# Revit family: NLRS_63_LF_UN_noodverlichting Hillux_htk
name_source: partatom
category: Lighting Fixtures
units: mm (PartAtom-declared; Revit-internal decimal feet)

## family parameters
Always vertical = No
Cut with Voids When Loaded = No
Light Source = Yes
OmniClass Number = 23.80.70.11.21
OmniClass Title = Emergency Lighting
Part Type = Normal
Room Calculation Point = No
Round Connector Dimension = Use Diameter
Shared = Yes
Work Plane-Based = No

## types (1)
- Hillux LED Series 3 dec AT opbouw_NMD720-3
    Color Filter = 16777215
    Default Elevation = 0 mm  [stored 0 ft]
    Dimming Lamp Color Temperature Shift = <None>
    Emit Shape Visible in Rendering = Yes
    Emit from Circle Diameter = 610 mm
    Lamp = LED
    Manufacturer = Hertek
    Model = Hillux LED
    NLRS_C_breedte = 118 mm
    NLRS_C_breedte1 = 111 mm
    NLRS_C_code_artikel = NMB720-3
    NLRS_C_code_fabrikant_gln = 8714253082646
    NLRS_C_content_datum_uitgifte = 01-08-2022
    NLRS_C_content_versie = 1.0
    NLRS_C_diameter = 0 mm  [stored 0 ft]
    NLRS_C_diepte = 0 mm  [stored 0 ft]
    NLRS_C_dikte = 277 mm  [stored 0.908793 ft]
    NLRS_C_garantie_termijn = 5 jaar op het armatuur en 4 jaar op de batterij
    NLRS_C_hoogte = 230 mm  [stored 0.754593 ft]
    NLRS_C_hoogte1 = 220 mm  [stored 0.721785 ft]
    NLRS_C_lengte = 0 mm  [stored 0 ft]
    NLRS_C_leverancier_bedrijfsnaam = Hertek
    NLRS_C_materiaal = Plastic, wit
    NLRS_C_materiaal_01 = Milk Glass
    NLRS_C_materiaal_kleur = wit
    NLRS_C_materiaal_kleur_01 = melkglas
    NLRS_C_omschrijving = Hillux LED series 3 dec AT opbouw
    NLRS_C_revit_versie = 2020
    NLRS_C_type_comments = Decentraal noodverlichtingarmatuur met volgende specificaties:
Type armatuur		: Hillux
Producent/leverancier	: Hertek
Functie			: Vluchtwegverlichting armatuur
Montagewijze		: Opbouw 
Voorzien van		: Volautomatische zelftest
Voedingsspanning	: 230VAC 
Functie			: continue/nood/nacht-nood
Opgenomen vermogen	: 11,5 Watt
Type lichtbron		: 5x high power LED
Kleurtemperatuur	: 3000K
Lichtstroom nominaal	: 690 Lumen
Lichtstroom in nood	: 600 Lumen
Autonomietijd		: 1 uur
Batterij			: NiMh 4,8V/4000mAh
Afmetingen		: 340x115 (b x h)
Gewicht		: 1,6 kg
Water- & stofdichtheid	: IP 65
Slagvastheid		: IK10
Garantie		: 5 jaar op het armatuur en 4 jaar op de batterij
    NLRS_E_spanning = 230 V
    NLRS_E_stroom = 0 A
    Omschrijving = Hillux LED series 3 dec AT opbouw
    Photometric Web File = MULTIHILL-LED-AT.1H_3000K_LDT.ies
    Tilt Angle = 90.00°
    Type Image = Hillux.jpg
    URL = https://www.hertek.nl
    Wattage Comments = 11,5W
    batterij type = Universeel batterij NiMH 4,8V/4000mAh aku0038

note: [stored X ft] marks values corroborated as IEEE doubles in the binary element streams (Revit-internal decimal feet)

## geometry (parser evidence)
native form markers: Blend x20, Sweep x18
no freeform markers — native parametric forms only
